# Revit family: Geräteeinsatz quadratisch für Estrichhöhe 55 mm
name_source: partatom
category: Generic Models
revit_build: Autodesk Revit 2015 (Build: 20140606_1530(x64)
units: mm (PartAtom-declared; Revit-internal decimal feet)

## types (2) — shared parameters
Height = 56 mm  [stored 0.183727 ft]
Height 1 = 3 mm  [stored 0.00984252 ft]
Length = 242 mm  [stored 0.793963 ft]
Length 1 = 264 mm  [stored 0.866142 ft]
Manufacturer = http://www.obo-bettermann.com
Width = 242 mm  [stored 0.793963 ft]
Width 1 = 264 mm  [stored 0.866142 ft]

## per-type parameters (varying)
| type | Article Type | GTIN | Manufacturer Art.No. | Material |
| GES9 55U V7011 | GES9 55U V 7011 | 4012195674436 | 7405037 | OBO PA, Eisengrau |
| GES9 55U V 9011 | GES9 55U V 9011 | 4012195674443 | 7405039 | OBO PA, Graphitschwarz |

note: [stored X ft] marks values corroborated as IEEE doubles in the binary element streams (Revit-internal decimal feet)

## geometry (parser evidence)
native form markers: Sweep x1
no freeform markers — native parametric forms only
